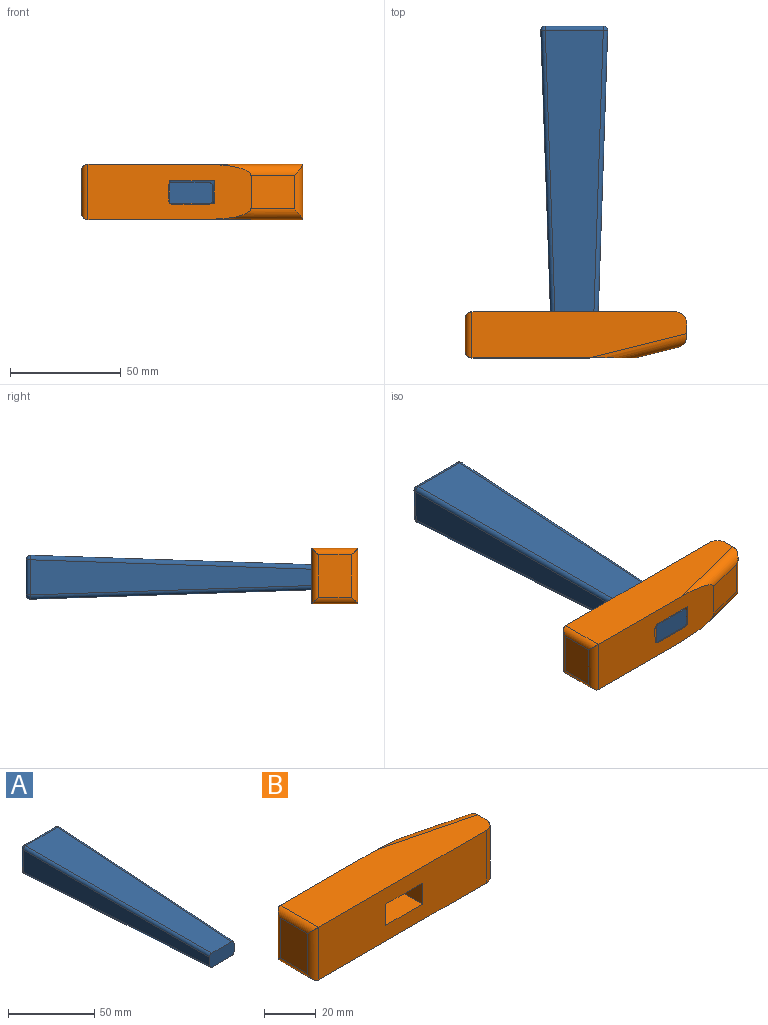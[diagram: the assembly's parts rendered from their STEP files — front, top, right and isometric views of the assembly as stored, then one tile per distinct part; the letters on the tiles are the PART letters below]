
ASSEMBLY  parts=2 mates=1
PART A: 18 faces, bbox 30.2x150x19.9 mm
  f0: plane 20.23x10mm, normal (0,-1,0), area 198mm2, adj f2,f3,f4,f5,f6,f8,f11,f14
  f1: plane 26.24x15.86mm, normal (0,1,0), area 412.6mm2, adj f7,f12,f13,f17
  f2: plane 147.93x15.86mm, normal (-1,-0.03,-0.03), area 1619mm2, adj f0,f8,f13,f14
  f3: plane 147.93x26.24mm, normal (0,-0.03,1), area 3143.4mm2, adj f0,f6,f7,f8
  f4: plane 147.93x15.86mm, normal (1,-0.03,0), area 1618.3mm2, adj f0,f6,f11,f12
  f5: plane 147.93x25.78mm, normal (0,-0.03,-1), area 3096.5mm2, adj f0,f11,f14,f17
  f6: cylinder r=2mm len=147.96mm, axis (0.03,1,0.03), area 464.9mm2, adj f0,f3,f4,f9
  f7: cylinder r=2mm len=26.24mm, axis (1,0,0), area 84.2mm2, adj f1,f3,f9,f10
  f8: cylinder r=2mm len=147.96mm, axis (-0.03,1,0.03), area 473.5mm2, adj f0,f2,f3,f10
  f9: sphere r=2mm, area 6.6mm2, adj f6,f7,f12
  f10: sphere r=2mm, area 6.7mm2, adj f7,f8,f13
  f11: cylinder r=2mm len=147.96mm, axis (0.03,1,-0.03), area 464.9mm2, adj f0,f4,f5,f15
  f12: cylinder r=2mm len=15.86mm, axis (0,0,-1), area 50.9mm2, adj f1,f4,f9,f15
  f13: cylinder r=2mm len=15.92mm, axis (-0.03,0,1), area 50.9mm2, adj f1,f2,f10,f16
  f14: cylinder r=2mm len=147.96mm, axis (-0.03,1,-0.03), area 456.3mm2, adj f0,f2,f5,f16
  f15: sphere r=2mm, area 6.6mm2, adj f11,f12,f17
  f16: sphere r=2mm, area 6.4mm2, adj f13,f14,f17
  f17: cylinder r=2mm len=25.78mm, axis (-1,0,0), area 82.7mm2, adj f1,f5,f15,f16
PART B: 19 faces, bbox 101.2x25.7x25 mm
  f0: plane 73.67x25mm, normal (0,1,0), area 1597.4mm2, adj f4,f5,f6,f7,f8,f9,f10,f12
  f1: plane 19x14.83mm, normal (-1,0,0), area 281.8mm2, adj f15,f16,f17,f18
  f2: plane 92x25mm, normal (0,-1,0), area 2100mm2, adj f5,f6,f7,f8,f9,f10,f11,f15
  f3: plane 25x6.1mm, normal (1,0,0), area 152.3mm2, adj f5,f6,f11,f12,f13,f14
  f4: plane 19.55x15mm, normal (0.24,0.97,0), area 302.2mm2, adj f0,f12,f13,f14
  f5: plane 97x20.83mm, normal (0,0,1), area 1774mm2, adj f0,f2,f3,f11,f12,f16
  f6: plane 97x20.83mm, normal (0,0,-1), area 1774mm2, adj f0,f2,f3,f11,f13,f17
  f7: plane 20.83x10mm, normal (1,0,0), area 208.3mm2, adj f0,f2,f8,f10
  f8: plane 20.83x20mm, normal (0,0,1), area 416.7mm2, adj f0,f2,f7,f9
  f9: plane 20.83x10mm, normal (-1,0,0), area 208.3mm2, adj f0,f2,f8,f10
  f10: plane 20.83x20mm, normal (0,0,-1), area 416.7mm2, adj f0,f2,f7,f9
  f11: cylinder r=5mm len=25mm, axis (0,0,-1), area 196.3mm2, adj f2,f3,f5,f6
  f12: cylinder r=5mm len=45.16mm, axis (0.97,-0.24,0), area 240.4mm2, adj f0,f3,f4,f5,f14
  f13: cylinder r=5mm len=45.16mm, axis (-0.97,0.24,0), area 240.4mm2, adj f0,f3,f4,f6,f14
  f14: cylinder r=5mm len=24.7mm, axis (0,0,-1), area 137.3mm2, adj f3,f4,f12,f13
  f15: cylinder r=3mm len=25mm, axis (0,0,-1), area 107.5mm2, adj f1,f2,f16,f17
  f16: cylinder r=3mm len=20.83mm, axis (0,1,0), area 87.9mm2, adj f1,f5,f15,f18
  f17: cylinder r=3mm len=20.83mm, axis (0,-1,0), area 87.9mm2, adj f1,f6,f15,f18
  f18: cylinder r=3mm len=25mm, axis (0,0,-1), area 107.5mm2, adj f0,f1,f16,f17
PLACE A t=(-133.48,-33.28,-92.3)mm
PLACE B rot(axis=(1,0,0),180deg) t=(-133.59,12.41,-35.68)mm
MATE planar B.f0 <-> A.f0  axis (0,-1,0) through (-114.7,-33.28,-53.18)mm
